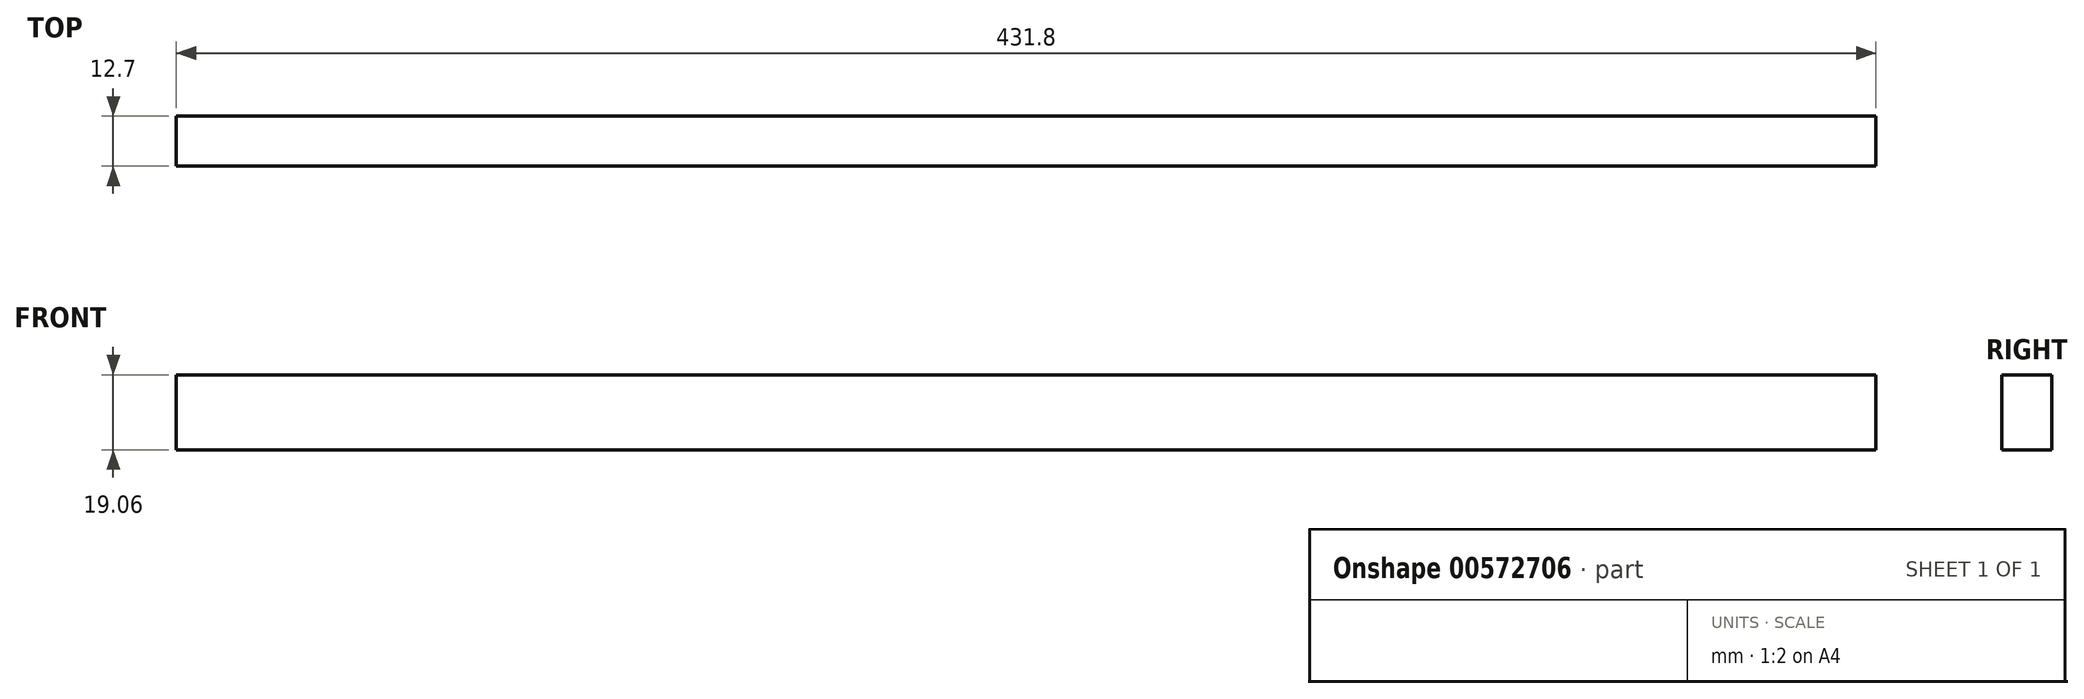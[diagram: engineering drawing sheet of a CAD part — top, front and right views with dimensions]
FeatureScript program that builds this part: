
annotation { "Feature Type Name" : "Feature", "Feature Type Description" : "" }
export const myFeature = defineFeature(function(context is Context, id is Id, definition is map)
    precondition{}
    {
        {
            var Q0;
            Q0=qCreatedBy(makeId("Top.planeOp"),FACE);
            var sketch = newSketch(context, id + "F0", { "sketchPlane" : qUnion([Q0])});
            skLineSegment(sketch, "E0.bottom", {"start": v(-215.9, 6.35) * mm, "end": v(215.9, 6.35) * mm});
            skLineSegment(sketch, "E0.top", {"start": v(-215.9, -6.35) * mm, "end": v(215.9, -6.35) * mm});
            skLineSegment(sketch, "E0.left", {"start": v(-215.9, 6.35) * mm, "end": v(-215.9, -6.35) * mm});
            skLineSegment(sketch, "E0.right", {"start": v(215.9, 6.35) * mm, "end": v(215.9, -6.35) * mm});
            skPoint(sketch, "E0.middle", {"position": v(0, 0) * mm});
            skSolve(sketch);
        }
        {
            var Q0;
            Q0 = qSketchRegion(id + "F0", true);
            extrude(context, id + "F1", {"entities" : qUnion([Q0]), "endBound" : BoundingType.SYMMETRIC, "depth" : 19.05 * mm, "offsetDistance" : 25.4 * mm});
        }
    });
